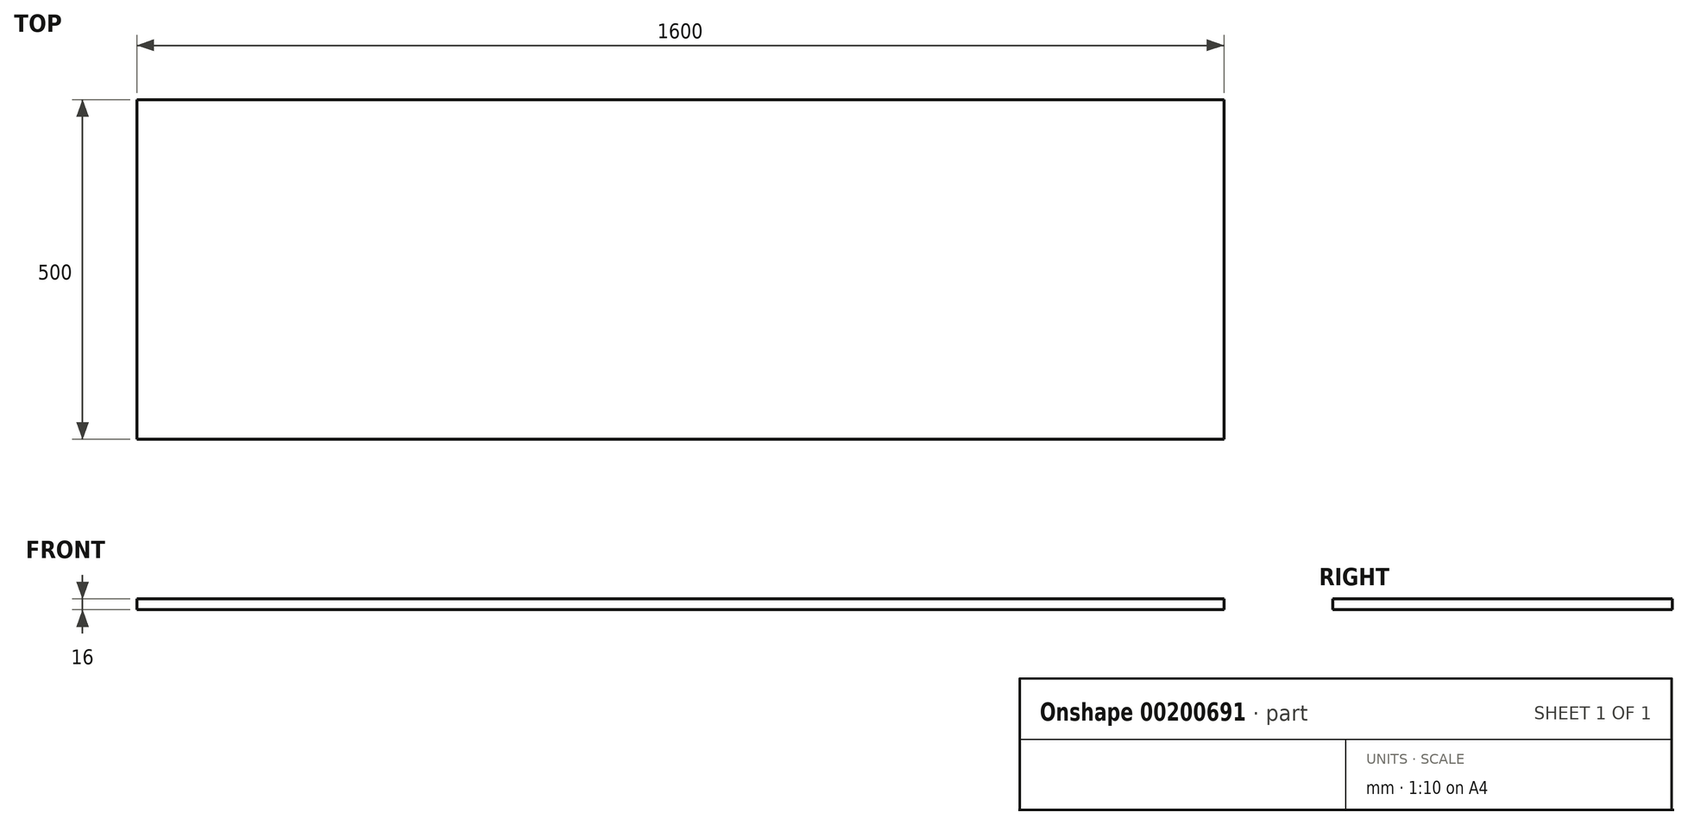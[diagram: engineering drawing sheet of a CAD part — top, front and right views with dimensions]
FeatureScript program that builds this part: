
annotation { "Feature Type Name" : "Feature", "Feature Type Description" : "" }
export const myFeature = defineFeature(function(context is Context, id is Id, definition is map)
    precondition{}
    {
        {
            var Q0;
            Q0=qCreatedBy(makeId("Front.planeOp"),FACE);
            var sketch = newSketch(context, id + "F0", { "sketchPlane" : qUnion([Q0])});
            skLineSegment(sketch, "E0.bottom", {"start": v(0, 0) * mm, "end": v(1600, 0) * mm});
            skLineSegment(sketch, "E0.top", {"start": v(0, 16) * mm, "end": v(1600, 16) * mm});
            skLineSegment(sketch, "E0.left", {"start": v(0, 0) * mm, "end": v(0, 16) * mm});
            skLineSegment(sketch, "E0.right", {"start": v(1600, 0) * mm, "end": v(1600, 16) * mm});
            skSolve(sketch);
        }
        {
            var Q0;
            Q0=qSketchRegion(id+"F0",true);
            extrude(context, id + "F1", {"entities" : qUnion([Q0]), "depth" : 500 * mm});
        }
    });
